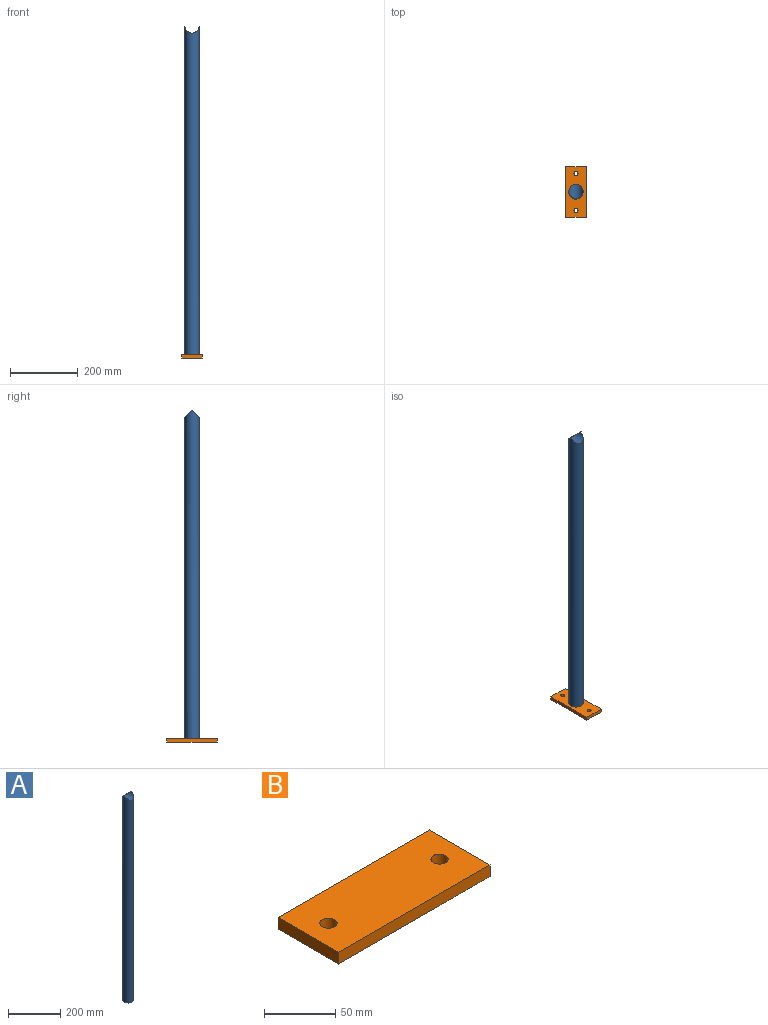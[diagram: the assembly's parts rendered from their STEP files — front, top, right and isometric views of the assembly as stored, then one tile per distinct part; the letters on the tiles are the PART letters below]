
ASSEMBLY  parts=2 mates=1
PART A: 3 faces, bbox 42x42.1x969 mm
  f0: cylinder r=21mm len=969mm, axis (0,0,1), area 126092.5mm2, adj f1,f2
  f1: plane 42x42mm, normal (0,0,-1), area 1385.4mm2, adj f0
  f2: cylinder r=21mm len=42.14mm, axis (0,1,0), area 1764mm2, adj f0
PART B: 8 faces, bbox 150x60x10 mm
  f0: plane 60x10mm, normal (1,0,0), area 600mm2, adj f1,f4,f6,f7
  f1: plane 150x10mm, normal (0,1,0), area 1500mm2, adj f0,f2,f6,f7
  f2: plane 60x10mm, normal (-1,0,0), area 600mm2, adj f1,f4,f6,f7
  f3: cylinder r=6mm len=12mm, axis (0,0,-1), area 377mm2, adj f6,f7
  f4: plane 150x10mm, normal (0,-1,0), area 1500mm2, adj f0,f2,f6,f7
  f5: cylinder r=6mm len=12mm, axis (0,0,-1), area 377mm2, adj f6,f7
  f6: plane 150x60mm, normal (0,0,1), area 8773.8mm2, adj f0,f1,f2,f3,f4,f5
  f7: plane 150x60mm, normal (0,0,-1), area 8773.8mm2, adj f0,f1,f2,f3,f4,f5
PLACE A t=(86.75,-165.36,161.33)mm
PLACE B rot(axis=(0,0,1),90deg) t=(86.75,-165.36,-817.67)mm
MATE fastened B.f6 <-> A.f0  axis (0,0,1) through (86.75,-165.36,-807.67)mm
